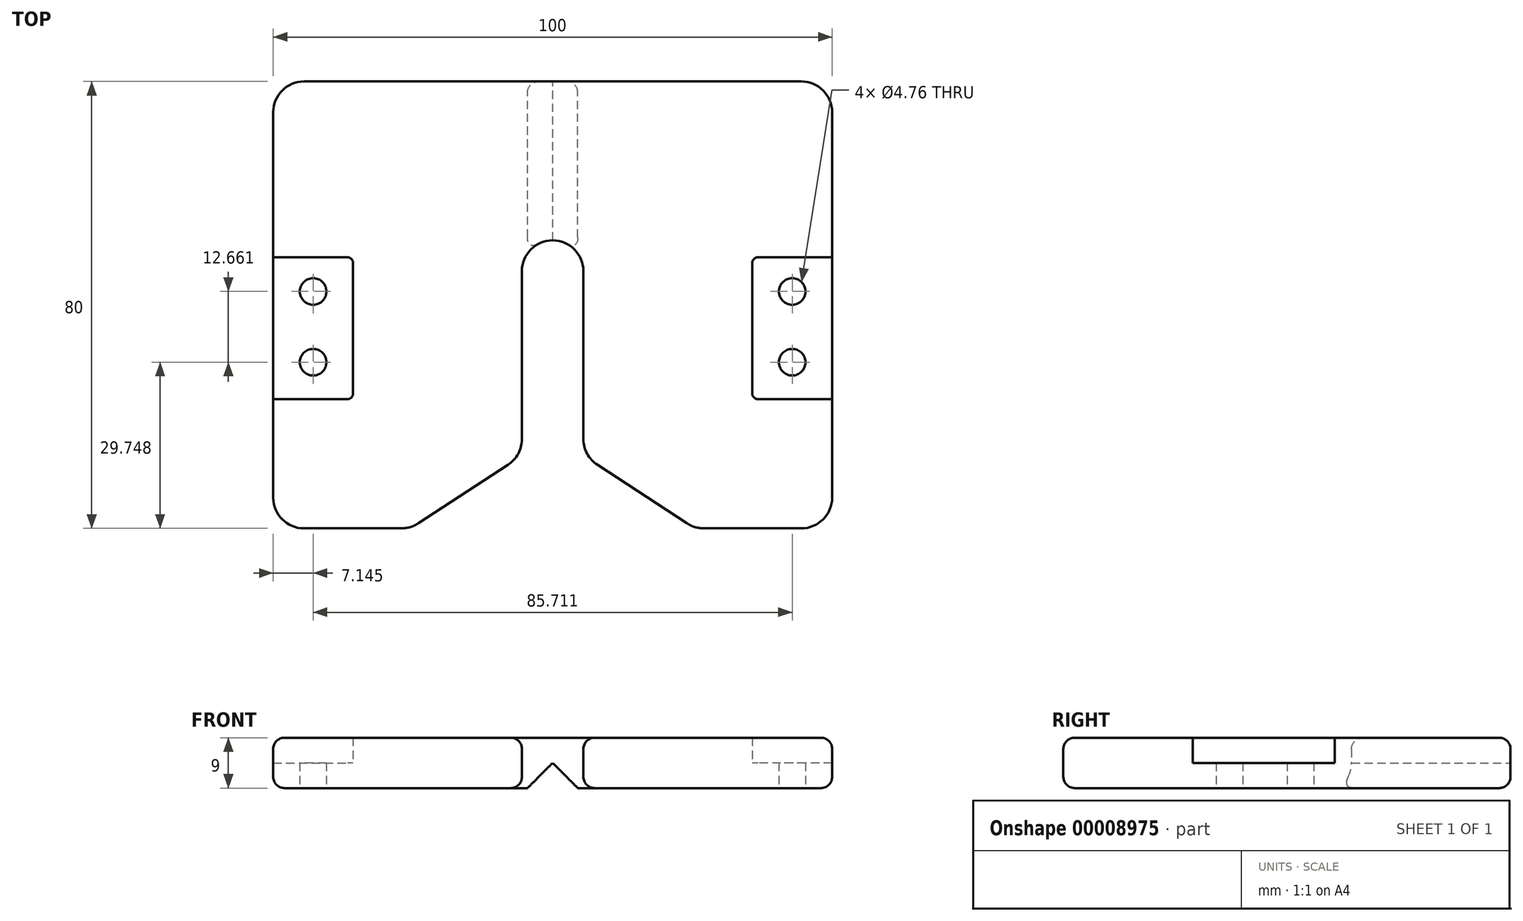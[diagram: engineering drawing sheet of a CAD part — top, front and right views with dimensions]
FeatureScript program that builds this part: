
annotation { "Feature Type Name" : "Feature", "Feature Type Description" : "" }
export const myFeature = defineFeature(function(context is Context, id is Id, definition is map)
    precondition{}
    {
        {
            var Q0;
            Q0=qCreatedBy(makeId("Top.planeOp"),FACE);
            var sketch = newSketch(context, id + "F0", { "sketchPlane" : qUnion([Q0])});
            skLineSegment(sketch, "E0.rect.bottom", {"start": v(44.5, 33.94) * mm, "end": v(-44.5, 33.94) * mm});
            skLineSegment(sketch, "E0.rect.top", {"start": v(44.5, -46.06) * mm, "end": v(27.05, -46.06) * mm});
            skLineSegment(sketch, "E0.rect.left", {"start": v(50, 28.44) * mm, "end": v(50, -40.56) * mm});
            skLineSegment(sketch, "E0.rect.right", {"start": v(-50, 28.44) * mm, "end": v(-50, -40.56) * mm});
            skPoint(sketch, "E0.rect.middle", {"position": v(0, -6.06) * mm});
            skLineSegment(sketch, "E1", {"start": v(0, -46.06) * mm, "end": v(0, 0) * mm, "construction": true});
            skArc(sketch, "E2", {"start": v(5.5, 0) * mm, "mid": v(0, 5.5) * mm, "end": v(-5.5, 0) * mm});
            skLineSegment(sketch, "E3", {"start": v(-5.5, 0) * mm, "end": v(-5.5, -30.08) * mm});
            skLineSegment(sketch, "E4", {"start": v(-8, -34.69) * mm, "end": v(-24.04, -45.16) * mm});
            skLineSegment(sketch, "E5", {"start": v(5.5, 0) * mm, "end": v(5.5, -30.08) * mm});
            skLineSegment(sketch, "E6", {"start": v(8, -34.69) * mm, "end": v(24.04, -45.16) * mm});
            skArc(sketch, "E7", {"start": v(5.5, -30.08) * mm, "mid": v(6.16, -32.7) * mm, "end": v(8, -34.69) * mm});
            skArc(sketch, "E8", {"start": v(-8, -34.69) * mm, "mid": v(-6.16, -32.7) * mm, "end": v(-5.5, -30.08) * mm});
            skArc(sketch, "E9", {"start": v(-44.5, 33.94) * mm, "mid": v(-48.39, 32.33) * mm, "end": v(-50, 28.44) * mm});
            skArc(sketch, "E10", {"start": v(50, 28.44) * mm, "mid": v(48.39, 32.33) * mm, "end": v(44.5, 33.94) * mm});
            skArc(sketch, "E11", {"start": v(24.04, -45.16) * mm, "mid": v(25.48, -45.83) * mm, "end": v(27.05, -46.06) * mm});
            skArc(sketch, "E12", {"start": v(44.5, -46.06) * mm, "mid": v(48.39, -44.45) * mm, "end": v(50, -40.56) * mm});
            skArc(sketch, "E13", {"start": v(-27.05, -46.06) * mm, "mid": v(-25.48, -45.83) * mm, "end": v(-24.04, -45.16) * mm});
            skArc(sketch, "E14", {"start": v(-50, -40.56) * mm, "mid": v(-48.39, -44.45) * mm, "end": v(-44.5, -46.06) * mm});
            skPoint(sketch, "E15.orphan", {"position": v(-50, -46.06) * mm});
            skLineSegment(sketch, "E16.trimOffspring", {"start": v(-27.05, -46.06) * mm, "end": v(-44.5, -46.06) * mm});
            skPoint(sketch, "E17.orphan", {"position": v(-5.5, -33.06) * mm});
            skPoint(sketch, "E18.orphan", {"position": v(5.5, -33.06) * mm});
            skPoint(sketch, "E19.orphan", {"position": v(25.41, -46.06) * mm});
            skPoint(sketch, "E20.orphan", {"position": v(-25.41, -46.06) * mm});
            skPoint(sketch, "E21.orphan", {"position": v(50, -46.06) * mm});
            skPoint(sketch, "E22.orphan", {"position": v(50, 33.94) * mm});
            skPoint(sketch, "E23.orphan", {"position": v(-50, 33.94) * mm});
            skLineSegment(sketch, "E24.bottom", {"start": v(-50, 2.47) * mm, "end": v(-35.71, 2.47) * mm});
            skLineSegment(sketch, "E24.top", {"start": v(-50, -22.93) * mm, "end": v(-35.71, -22.93) * mm});
            skLineSegment(sketch, "E24.left", {"start": v(-50, 2.47) * mm, "end": v(-50, -22.93) * mm});
            skLineSegment(sketch, "E24.right", {"start": v(-35.71, 2.47) * mm, "end": v(-35.71, -22.93) * mm});
            skLineSegment(sketch, "E25.0.MirrorCS", {"start": v(35.71, 2.47) * mm, "end": v(35.71, -22.93) * mm});
            skLineSegment(sketch, "E25.1.MirrorCS", {"start": v(50, -22.93) * mm, "end": v(35.71, -22.93) * mm});
            skLineSegment(sketch, "E25.2.MirrorCS", {"start": v(50, 2.47) * mm, "end": v(50, -22.93) * mm});
            skLineSegment(sketch, "E25.3.MirrorCS", {"start": v(50, 2.47) * mm, "end": v(35.71, 2.47) * mm});
            skCircle(sketch, "E26", {"center": v(-42.86, -3.65) * mm, "radius": 2.38 * mm});
            skCircle(sketch, "E27", {"center": v(-42.86, -16.31) * mm, "radius": 2.38 * mm});
            skLineSegment(sketch, "E28.bottom", {"start": v(-3.6, -0.23) * mm, "end": v(3.4, -0.23) * mm, "construction": true});
            skLineSegment(sketch, "E28.top", {"start": v(-3.6, -20.23) * mm, "end": v(3.4, -20.23) * mm, "construction": true});
            skLineSegment(sketch, "E28.left", {"start": v(-3.6, -0.23) * mm, "end": v(-3.6, -20.23) * mm, "construction": true});
            skLineSegment(sketch, "E28.right", {"start": v(3.4, -0.23) * mm, "end": v(3.4, -20.23) * mm, "construction": true});
            skLineSegment(sketch, "E29", {"start": v(-35.71, -10.23) * mm, "end": v(-3.6, -10.23) * mm, "construction": true});
            skLineSegment(sketch, "E30", {"start": v(3.4, -10.23) * mm, "end": v(35.71, -10.23) * mm, "construction": true});
            skCircle(sketch, "E31.0.MirrorC", {"center": v(42.86, -3.65) * mm, "radius": 2.38 * mm});
            skCircle(sketch, "E32.0.MirrorC", {"center": v(42.86, -16.31) * mm, "radius": 2.38 * mm});
            skLineSegment(sketch, "E33", {"start": v(-42.86, 2.47) * mm, "end": v(-42.86, -22.93) * mm, "construction": true});
            skSolve(sketch);
        }
        {
            var Q0;
            Q0=makeQuery(id+"F0.imprint","IMPRINT",FACE,{"disambiguationData":[TD([[makeQuery(id+"F0.imprint","IMPRINT",EDGE,{"derivedFrom":sQuery(id+"F0.wireOp",EDGE,"E0.rect.bottom")}),1.0]])]});
            var Q1;
            Q1=makeQuery(id+"F0.imprint","IMPRINT",FACE,{"disambiguationData":[TD([[makeQuery(id+"F0.imprint","IMPRINT",EDGE,{"derivedFrom":sQuery(id+"F0.wireOp",EDGE,"E24.bottom")}),-1.0]])]});
            var Q2;
            Q2=makeQuery(id+"F0.imprint","IMPRINT",FACE,{"disambiguationData":[TD([[makeQuery(id+"F0.imprint","IMPRINT",EDGE,{"derivedFrom":sQuery(id+"F0.wireOp",EDGE,"E25.0.MirrorCS")}),1.0]])]});
            extrude(context, id + "F1", {"entities" : qUnion([Q0, Q1, Q2]), "depth" : 9 * mm, "symmetric" : true});
        }
        {
            var Q0;
            Q0=makeQuery(id+"F1.opExtrude","SWEPT_FACE",FACE,{"disambiguationData":[OSD([sQuery(id+"F0.wireOp",EDGE,"E0.rect.bottom")])]});
            var sketch = newSketch(context, id + "F2", { "sketchPlane" : qUnion([Q0])});
            skLineSegment(sketch, "E34", {"start": v(0, 0) * mm, "end": v(-4.5, -4.5) * mm});
            skLineSegment(sketch, "E35", {"start": v(0, 0) * mm, "end": v(0, -4.5) * mm, "construction": true});
            skLineSegment(sketch, "E36.0.MirrorCS", {"start": v(0, 0) * mm, "end": v(4.5, -4.5) * mm});
            skLineSegment(sketch, "E37", {"start": v(-4.5, -4.5) * mm, "end": v(4.5, -4.5) * mm});
            skSolve(sketch);
        }
        {
            var Q0;
            Q0 = qSketchRegion(id + "F2", true);
            extrude(context, id + "F3", {"entities" : qUnion([Q0]), "operationType" : NewBodyOperationType.REMOVE, "endBound" : BoundingType.THROUGH_ALL, "oppositeDirection" : true, "depth" : 25 * mm});
        }
        {
            var Q0;
            Q0=makeQuery(id+"F1.opExtrude","CAP_EDGE",EDGE,{"disambiguationData":[OSD([sQuery(id+"F0.wireOp",EDGE,"E0.rect.right")])],"isStart":false});
            var Q1;
            Q1=makeQuery(id+"F1.opExtrude","CAP_EDGE",EDGE,{"disambiguationData":[OSD([sQuery(id+"F0.wireOp",EDGE,"E0.rect.right")])],"isStart":true});
            var Q2;
            Q2=makeQuery(id+"F3.boolean.opBoolean","COPY",EDGE,{"derivedFrom":makeQuery(id+"F3.opExtrude","SWEPT_EDGE",EDGE,{"disambiguationData":[OSD([sQuery(id+"F0.wireOp",EDGE,"E0.rect.bottom"),sQuery(id+"F2.wireOp",EDGE,"E36.0.MirrorCS"),sQuery(id+"F2.wireOp",EDGE,"E37")])]})});
            var Q3;
            Q3=makeQuery(id+"F3.boolean.opBoolean","COPY",EDGE,{"derivedFrom":makeQuery(id+"F3.opExtrude","SWEPT_EDGE",EDGE,{"disambiguationData":[OSD([sQuery(id+"F0.wireOp",EDGE,"E0.rect.bottom"),sQuery(id+"F2.wireOp",EDGE,"E34"),sQuery(id+"F2.wireOp",EDGE,"E37")])]})});
            var Q4;
            Q4=makeQuery(id+"F1.opExtrude","CAP_EDGE",EDGE,{"disambiguationData":[OSD([sQuery(id+"F0.wireOp",EDGE,"E0.rect.left")])],"isStart":true});
            fillet(context, id + "F4", {"entities" : qUnion([Q0, Q1, Q2, Q3, Q4]), "radius" : 2 * mm, "tangentPropagation" : true, "allowEdgeOverflow" : false});
        }
        {
            var Q0;
            Q0=makeQuery(id+"F0.imprint","IMPRINT",FACE,{"disambiguationData":[TD([[makeQuery(id+"F0.imprint","IMPRINT",EDGE,{"derivedFrom":sQuery(id+"F0.wireOp",EDGE,"E24.bottom")}),-1.0]])]});
            var Q1;
            Q1=makeQuery(id+"F0.imprint","IMPRINT",FACE,{"disambiguationData":[TD([[makeQuery(id+"F0.imprint","IMPRINT",EDGE,{"derivedFrom":sQuery(id+"F0.wireOp",EDGE,"E25.0.MirrorCS")}),1.0]])]});
            extrude(context, id + "F5", {"entities" : qUnion([Q0, Q1]), "operationType" : NewBodyOperationType.REMOVE, "depth" : 4.5 * mm});
        }
        {
            var Q0;
            Q0=makeQuery(id+"F5.boolean.opBoolean","COPY",EDGE,{"derivedFrom":makeQuery(id+"F5.opExtrude","SWEPT_EDGE",EDGE,{"disambiguationData":[OSD([sQuery(id+"F0.wireOp",EDGE,"E25.0.MirrorCS"),sQuery(id+"F0.wireOp",EDGE,"E25.1.MirrorCS")])]})});
            var Q1;
            Q1=makeQuery(id+"F5.boolean.opBoolean","COPY",EDGE,{"derivedFrom":makeQuery(id+"F5.opExtrude","SWEPT_EDGE",EDGE,{"disambiguationData":[OSD([sQuery(id+"F0.wireOp",EDGE,"E25.0.MirrorCS"),sQuery(id+"F0.wireOp",EDGE,"E25.3.MirrorCS")])]})});
            var Q2;
            Q2=makeQuery(id+"F5.boolean.opBoolean","COPY",EDGE,{"derivedFrom":makeQuery(id+"F5.opExtrude","SWEPT_EDGE",EDGE,{"disambiguationData":[OSD([sQuery(id+"F0.wireOp",EDGE,"E24.top"),sQuery(id+"F0.wireOp",EDGE,"E24.right")])]})});
            var Q3;
            Q3=makeQuery(id+"F5.boolean.opBoolean","COPY",EDGE,{"derivedFrom":makeQuery(id+"F5.opExtrude","SWEPT_EDGE",EDGE,{"disambiguationData":[OSD([sQuery(id+"F0.wireOp",EDGE,"E24.bottom"),sQuery(id+"F0.wireOp",EDGE,"E24.right")])]})});
            fillet(context, id + "F6", {"entities" : qUnion([Q0, Q1, Q2, Q3]), "radius" : 1 * mm, "tangentPropagation" : true, "allowEdgeOverflow" : false});
        }
    });
